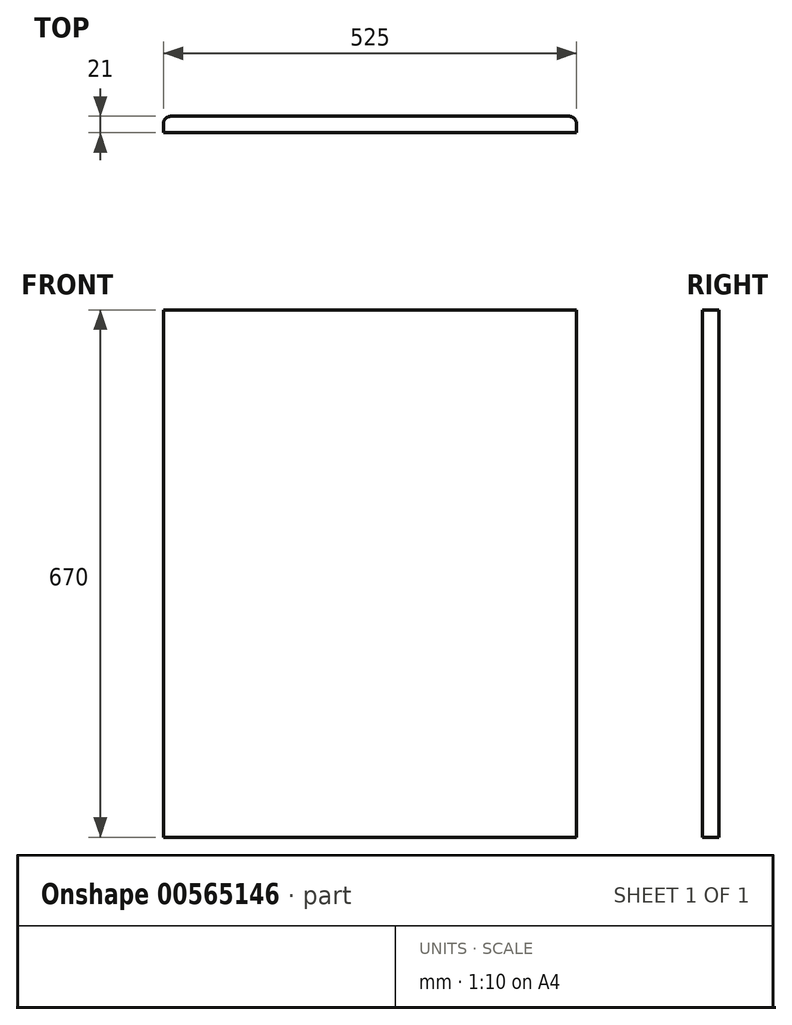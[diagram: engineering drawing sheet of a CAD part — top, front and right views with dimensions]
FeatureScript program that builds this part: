
annotation { "Feature Type Name" : "Feature", "Feature Type Description" : "" }
export const myFeature = defineFeature(function(context is Context, id is Id, definition is map)
    precondition{}
    {
        {
            var Q0;
            Q0=qCreatedBy(makeId("Front.planeOp"),FACE);
            var sketch = newSketch(context, id + "F0", { "sketchPlane" : qUnion([Q0])});
            skLineSegment(sketch, "E0.bottom", {"start": v(-262.5, 335) * mm, "end": v(262.5, 335) * mm});
            skLineSegment(sketch, "E0.top", {"start": v(-262.5, -335) * mm, "end": v(262.5, -335) * mm});
            skLineSegment(sketch, "E0.left", {"start": v(-262.5, 335) * mm, "end": v(-262.5, -335) * mm});
            skLineSegment(sketch, "E0.right", {"start": v(262.5, 335) * mm, "end": v(262.5, -335) * mm});
            skPoint(sketch, "E0.middle", {"position": v(0, 0) * mm});
            skSolve(sketch);
        }
        {
            var Q0;
            Q0 = qSketchRegion(id + "F0", true);
            var Q1;
            Q1=makeQuery(id+"F0.imprint","IMPRINT",FACE,{"disambiguationData":[TD([[makeQuery(id+"F0.imprint","IMPRINT",EDGE,{"derivedFrom":sQuery(id+"F0.wireOp",EDGE,"E0.bottom")}),-1.0]])]});
            extrude(context, id + "F1", {"entities" : qUnion([Q0, Q1]), "depth" : 21 * mm, "offsetDistance" : 25 * mm});
        }
        {
            var Q0;
            Q0=makeQuery(id+"F1.opExtrude","CAP_EDGE",EDGE,{"disambiguationData":[OSD([sQuery(id+"F0.wireOp",EDGE,"E0.left")])],"isStart":true});
            var Q1;
            Q1=makeQuery(id+"F1.opExtrude","CAP_EDGE",EDGE,{"disambiguationData":[OSD([sQuery(id+"F0.wireOp",EDGE,"E0.right")])],"isStart":true});
            fillet(context, id + "F2", {"entities" : qUnion([Q0, Q1]), "radius" : 10 * mm, "tangentPropagation" : true, "allowEdgeOverflow" : false});
        }
    });
